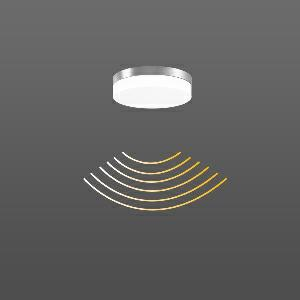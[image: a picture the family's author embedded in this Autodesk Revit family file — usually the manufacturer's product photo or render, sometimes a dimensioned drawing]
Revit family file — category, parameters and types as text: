
# Revit family: flat_slim_round_312135_004_2_191_4c50
name_source: partatom
category: Lighting Fixtures
units: mm (PartAtom-declared; Revit-internal decimal feet)

## family parameters
Cut with Voids When Loaded = No
Host = Face
Light Source = No
Part Type = Normal
Room Calculation Point = No
Round Connector Dimension = Use Diameter
Shared = No

## types (1)
- FLAT SLIM round (1 x LED Modul 830, 1300 lm, 3000)
    Apparent Load = 13 VA
    CIE Flux Codes = 43 74 92 91 100
    Color Rendering = 80
    Color Temperature = 3000
    Default Elevation = 1800 mm
    Height = 63 mm
    Lamp = 1 x LED Modul 830
    Lamp Light Flux = 1300 lm
    Lamp count = 1
    Length = 230 mm
    Lifetime = 50000 h
    Luminous efficacy = 100 lm/W
    Manufacturer = RZB
    ModVariant = No
    Model = 312135.004.2.191
    Mounting Place = Ceiling, Wall
    Mounting Type = Surface mounted
    Number of Poles = 1
    OnlyDefault = Yes
    Power Factor = 1
    Product Name = FLAT SLIM round
    Product group = Surface mounted ceiling and wall luminaires
    ProductGroupID = 305
    Protection Class = Protection class I
    Protection Degree = IP 65
    RLX_Detail_Level = 1
    RLX_Emergency_Light_Flux = 0 lm
    RLX_Emergency_Type = 0
    RLX_Emergency_Type_DB = No
    RlxData = <blob elided: 31289 chars, md5=a9b17b49>
    Socket = socket
    Standby Power = 0 W
    System Light Flux = 1300 lm
    System Power = 13 W
    Type Comments = Product without accessories
    Type Image = 312132.004.19.jpg
    URL = http://relux.com
    VarID = ---
    Voltage = 230 V
    Voltage Range = 220-240 V
    Weight = 0.00 kg
    Width = 0 mm  [stored 0 ft]

note: [stored X ft] marks values corroborated as IEEE doubles in the binary element streams (Revit-internal decimal feet)

## geometry (parser evidence)
native form markers: Blend x4, Sweep x11
no freeform markers — native parametric forms only
